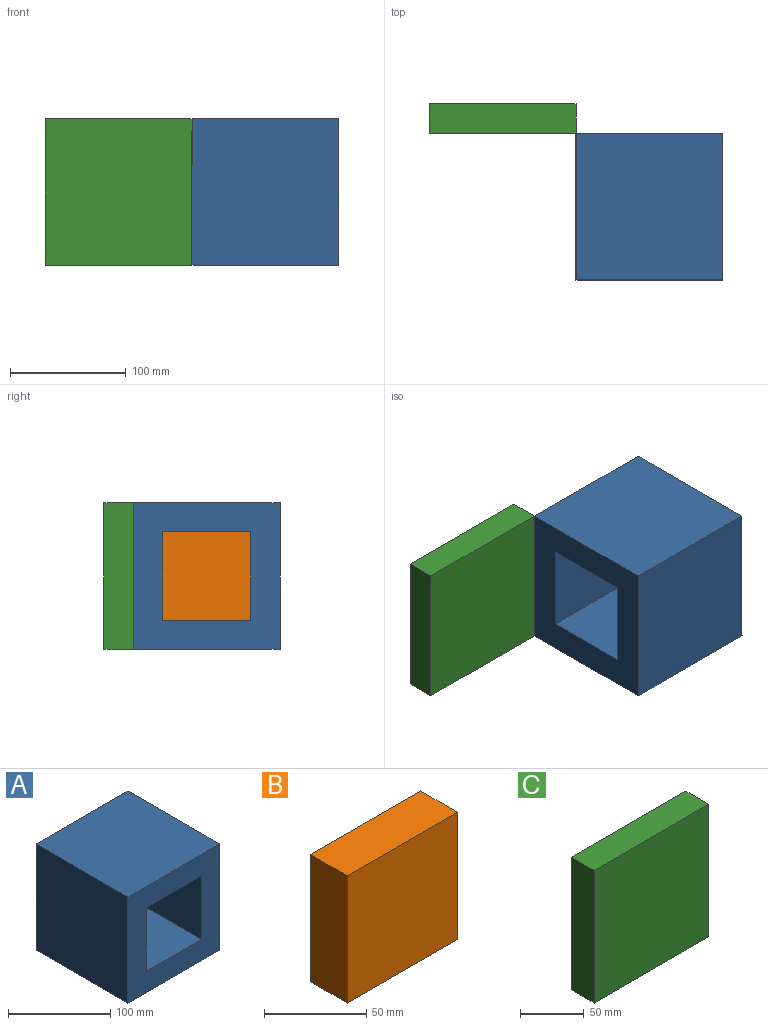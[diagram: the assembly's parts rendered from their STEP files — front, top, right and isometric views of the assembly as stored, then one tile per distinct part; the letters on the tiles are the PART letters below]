
ASSEMBLY  parts=3 mates=2
PART A: 10 faces, bbox 127x127x127 mm
  f0: plane 127x127mm, normal (0,0,1), area 16129mm2, adj f1,f7,f8,f9
  f1: plane 127x127mm, normal (-1,0,0), area 16129mm2, adj f0,f2,f8,f9
  f2: plane 127x127mm, normal (0,0,-1), area 16129mm2, adj f1,f7,f8,f9
  f3: plane 127x76.2mm, normal (0,0,1), area 9677.4mm2, adj f4,f6,f8,f9
  f4: plane 127x76.2mm, normal (1,0,0), area 9677.4mm2, adj f3,f5,f8,f9
  f5: plane 127x76.2mm, normal (0,0,-1), area 9677.4mm2, adj f4,f6,f8,f9
  f6: plane 127x76.2mm, normal (-1,0,0), area 9677.4mm2, adj f3,f5,f8,f9
  f7: plane 127x127mm, normal (1,0,0), area 16129mm2, adj f0,f2,f8,f9
  f8: plane 127x127mm, normal (0,1,0), area 10322.6mm2, adj f0,f1,f2,f3,f4,f5,f6,f7
  f9: plane 127x127mm, normal (0,-1,0), area 10322.6mm2, adj f0,f1,f2,f3,f4,f5,f6,f7
PART B: 6 faces, bbox 76.2x25.4x76.2 mm
  f0: plane 76.2x25.4mm, normal (0,0,1), area 1935.5mm2, adj f1,f3,f4,f5
  f1: plane 76.2x25.4mm, normal (-1,0,0), area 1935.5mm2, adj f0,f2,f4,f5
  f2: plane 76.2x25.4mm, normal (0,0,-1), area 1935.5mm2, adj f1,f3,f4,f5
  f3: plane 76.2x25.4mm, normal (1,0,0), area 1935.5mm2, adj f0,f2,f4,f5
  f4: plane 76.2x76.2mm, normal (0,1,0), area 5806.4mm2, adj f0,f1,f2,f3
  f5: plane 76.2x76.2mm, normal (0,-1,0), area 5806.4mm2, adj f0,f1,f2,f3
PART C: 6 faces, bbox 127x25.4x127 mm
  f0: plane 127x25.4mm, normal (-1,0,0), area 3225.8mm2, adj f1,f3,f4,f5
  f1: plane 127x25.4mm, normal (0,0,-1), area 3225.8mm2, adj f0,f2,f4,f5
  f2: plane 127x25.4mm, normal (1,0,0), area 3225.8mm2, adj f1,f3,f4,f5
  f3: plane 127x25.4mm, normal (0,0,1), area 3225.8mm2, adj f0,f2,f4,f5
  f4: plane 127x127mm, normal (0,-1,0), area 16129mm2, adj f0,f1,f2,f3
  f5: plane 127x127mm, normal (0,1,0), area 16129mm2, adj f0,f1,f2,f3
PLACE A rot(axis=(0.71,0.71,0),180deg) t=(242.08,37.13,-130.66)mm
PLACE B rot(axis=(0.71,-0.71,0),180deg) t=(369.08,37.13,-130.66)mm
PLACE C rot(axis=(0.71,0,-0.71),180deg) t=(179.04,100.63,-125.22)mm
MATE fastened B.f0 <-> A.f5  axis (0,0,-1) through (356.38,37.13,-168.76)mm
MATE revolute A.f7 <-> C.f5  axis (0,1,0) through (242.08,100.63,-130.66)mm
